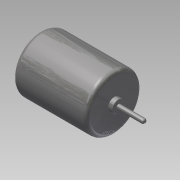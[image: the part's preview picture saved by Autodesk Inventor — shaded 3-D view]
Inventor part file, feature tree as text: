
AUTODESK INVENTOR PART (.ipt)
format: ipt  version: 2015 SP1 (Build 190203100, 203)  size: 616,448 bytes
history: native  units: mm
features: extrude x7, sketch x5, fillet x5
ambient origin geometry x8: Origin, YZ Plane, XZ Plane, XY Plane, X Axis, Y Axis, Z Axis, Center Point
bodies: Solid1 (feature_tree)
feature tree (17):
  sketch  "Sketch1"  dims[d0=25.37mm d1=5.66mm]
  extrude  "Extrusion1"  Depth=5.66mm
  extrude  "Extrusion2"  Depth=33.86mm TaperAngle=0.0deg
  extrude  "Extrusion3"  Depth=14.28mm TaperAngle=0.0deg
  fillet  "Fillet1"  Radius=2.0mm
  fillet  "Fillet2"  Radius=0.25mm
  fillet  "Fillet3"  Radius=1.0mm
  sketch  "Sketch2"  dims[d2=2.1mm d3=33.86mm d4=0.0mm]
  extrude  "Extrusion4"  Depth=2.0mm TaperAngle=0.0deg
  extrude  "Extrusion5"  Depth=0.25mm
  fillet  "Fillet4"  Radius=1.0mm
  fillet  "Fillet5"  Radius=10.0mm
  extrude  "Extrusion6"  Depth=10.0mm TaperAngle=0.0deg
  extrude  "Extrusion7"  [1 undecoded]
  sketch  "Sketch6"  dims[d15=2.62mm d16=0.0mm d17=0.25mm d18=1.0mm d19=10.0mm d20=0.0mm d21=10.0mm d22=0.0mm]
  sketch  "Sketch4"  dims[d5=2.0mm d6=0.0mm d7=14.28mm d8=0.0mm d9=2.0mm d10=0.25mm d11=1.0mm]
  sketch  "Sketch5"  dims[d12=2.0mm d13=2.0mm d14=0.0mm]
note: 1 required parameter value undecoded (feature->parameter linkage not recoverable at this tier; creation-order binding heuristic only, values carry confidence <= 0.55)
